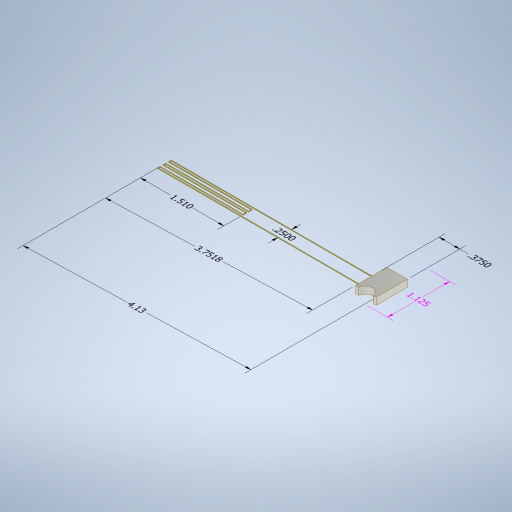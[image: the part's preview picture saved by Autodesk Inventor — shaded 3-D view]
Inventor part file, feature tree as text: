
AUTODESK INVENTOR PART (.ipt)
format: ipt  version: 2024.2 (Build 282272000, 272)  size: 361,472 bytes
history: native  units: in
note: dims shown in document units (in); Inventor stores cm internally (conversion verified against a paired STEP export)
features: other x7, sketch x5, extrude x3, plane x2, fillet x2, sweep x1
ambient origin geometry x8: Origin, YZ Plane, XZ Plane, XY Plane, X Axis, Y Axis, Z Axis, Center Point
bodies: Solid1 (feature_tree)
feature tree (20):
  other  "Annotations"
  sweep  "Sweep1"
  plane  "Work Plane1"
  plane  "Work Plane2"
  extrude  "Extrusion4"  Depth=0.05in
  fillet  "Fillet1"  Radius=0.05in
  extrude  "Extrusion5"  TaperAngle=0.0deg  [1 undecoded]
  fillet  "Fillet2"  Radius=0.05in
  extrude  "Extrusion6"  Depth=0.375in
  sketch  "Sketch1"  dims[d0=3.75in d1=0.05in]
  sketch  "Sketch2"  dims[d2=1.5in d3=0.05in d4=0.05in]
  sketch  "Sketch6"  dims[d5=0.05in d6=0.0in d7=0.0in]
  sketch  "Sketch7"  dims[d11=0.25in d19=-0.25in d22=1.5in d23=0.05in]
  sketch  "Sketch8"  dims[d24=0.01in d25=1.125in d26=0.375in d28=0.1875in d29=0.0in d30=0.125in d31=0.0in d32=0.125in d33=0.26in d34=0.26in d35=0.75in d36=0.1875in d37=0.125in d38=0.0in d39=0.185in d40=0.185in d41=0.125in d60=0.2in d61=0.0in d62=0.0in d63=0.01in d42=0.2341in d43=0.169in d44=0.25in d45=0.2391in d46=0.1704in d47=3.7518in d48=0.2141in d49=0.2512in d50=1.51in d51=0.1604in d52=0.1602in d53=0.375in d54=0.248in d55=0.2288in d56=1.125in d57=0.229in d58=0.216in d59=4.1266in]
  other  "Linear Dimension 1"
  other  "Linear Dimension 2"
  other  "Linear Dimension 3"
  other  "Linear Dimension 4"
  other  "Linear Dimension 5"
  other  "Linear Dimension 6"
note: 1 required parameter value undecoded (feature->parameter linkage not recoverable at this tier; creation-order binding heuristic only, values carry confidence <= 0.55)
